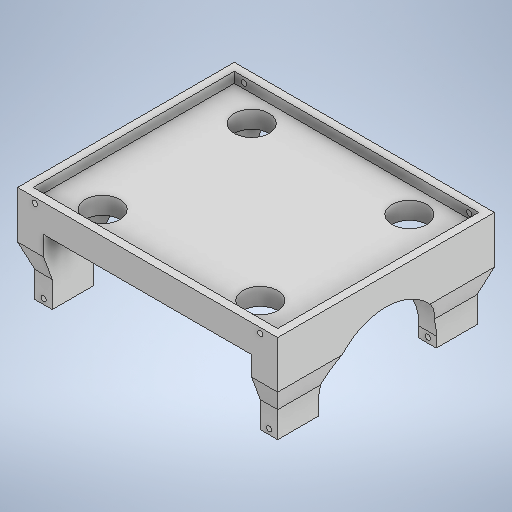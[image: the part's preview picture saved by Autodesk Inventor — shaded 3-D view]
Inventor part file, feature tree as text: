
AUTODESK INVENTOR PART (.ipt)
format: ipt  version: 2025.3 (Build 293356000, 356)  size: 345,088 bytes
history: native  units: mm
features: extrude x6, sketch x5, projected_geometry x3, other x1
ambient origin geometry x8: Origin, YZ Plane, XZ Plane, XY Plane, X Axis, Y Axis, Z Axis, Center Point
bodies: Body1 (feature_tree), Body2 (feature_tree)
feature tree (15):
  other  "솔리드1"
  extrude  "돌출1"  Depth=150.0mm
  extrude  "돌출2"  Depth=15.0mm
  sketch  "스케치3"
  extrude  "돌출3"  Depth=15.0mm
  extrude  "돌출4"  Depth=10.0mm
  extrude  "돌출6"  Depth=50.0mm
  extrude  "돌출7"  Depth=125.0mm TaperAngle=0.0deg
  sketch  "스케치1"
  sketch  "스케치2"
  projected_geometry  "투영된 루프1"
  projected_geometry  "투영된 루프2"
  projected_geometry  "투영된 루프3"
  sketch  "스케치5"
  sketch  "스케치6"
